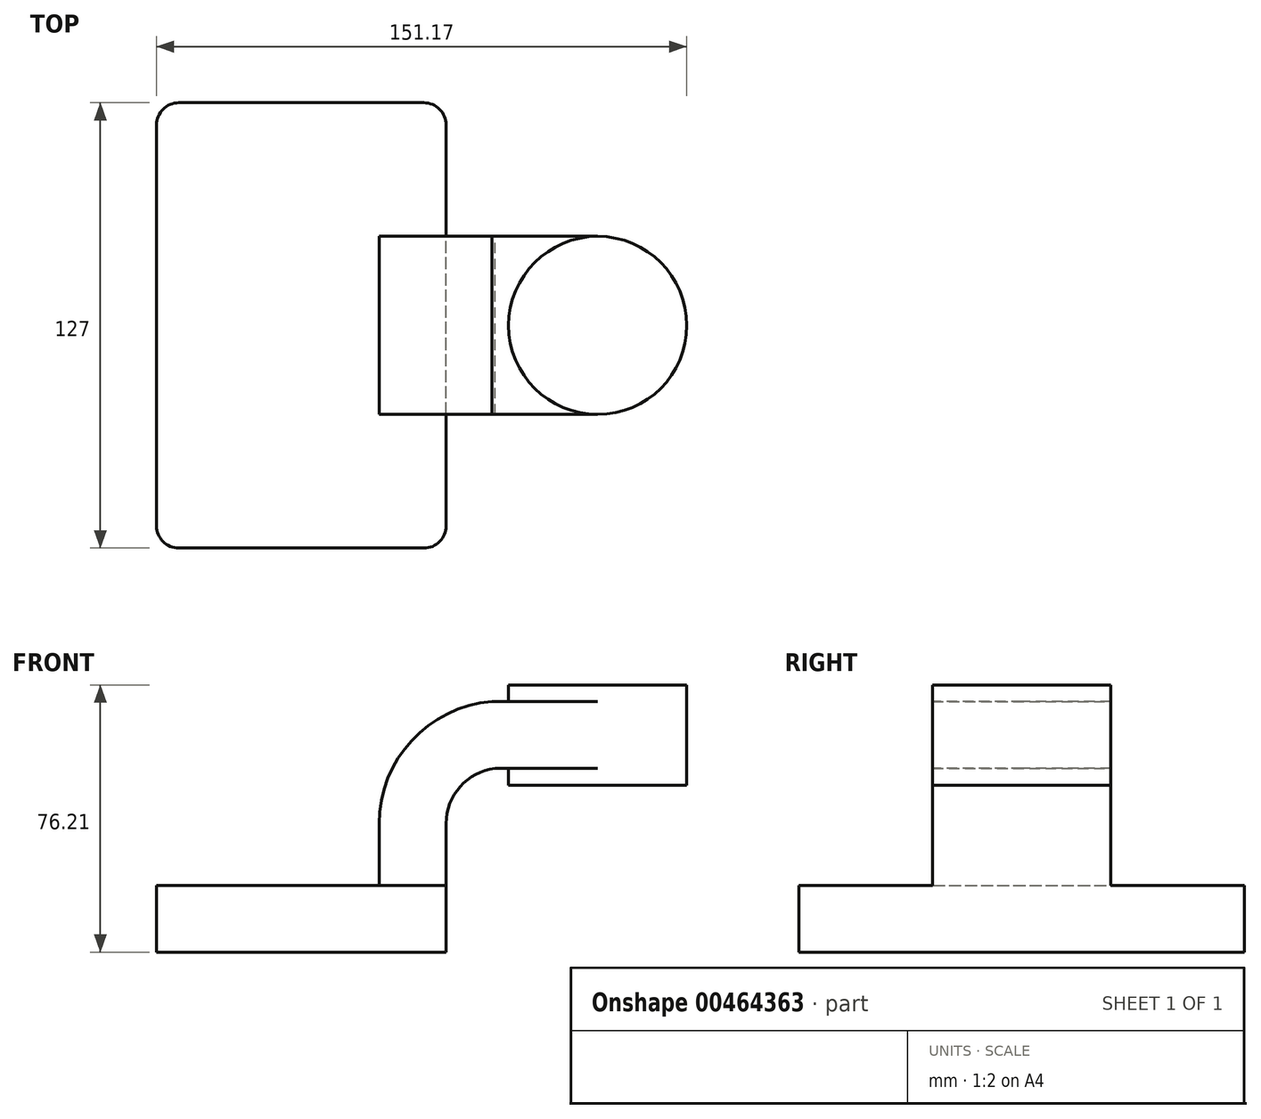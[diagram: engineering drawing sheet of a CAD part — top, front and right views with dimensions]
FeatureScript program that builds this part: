
annotation { "Feature Type Name" : "Feature", "Feature Type Description" : "" }
export const myFeature = defineFeature(function(context is Context, id is Id, definition is map)
    precondition{}
    {
        {
            var Q0;
            Q0=qCreatedBy(makeId("Front.planeOp"),FACE);
            var sketch = newSketch(context, id + "F0", { "sketchPlane" : qUnion([Q0])});
            skLineSegment(sketch, "E0.bottom", {"start": v(41.27, 9.53) * mm, "end": v(-41.28, 9.53) * mm});
            skLineSegment(sketch, "E0.top", {"start": v(41.28, -9.52) * mm, "end": v(-41.27, -9.52) * mm});
            skLineSegment(sketch, "E0.left", {"start": v(41.28, 9.53) * mm, "end": v(41.28, -9.52) * mm});
            skLineSegment(sketch, "E0.right", {"start": v(-41.28, 9.53) * mm, "end": v(-41.27, -9.52) * mm});
            skPoint(sketch, "E0.middle", {"position": v(0, 0) * mm});
            skLineSegment(sketch, "E1.bottom", {"start": v(109.9, 38.1) * mm, "end": v(59.1, 38.1) * mm});
            skLineSegment(sketch, "E1.top", {"start": v(109.9, 66.68) * mm, "end": v(59.1, 66.68) * mm});
            skLineSegment(sketch, "E1.left", {"start": v(109.9, 38.1) * mm, "end": v(109.9, 66.68) * mm});
            skLineSegment(sketch, "E1.right", {"start": v(59.1, 38.1) * mm, "end": v(59.1, 66.68) * mm});
            skPoint(sketch, "E1.middle", {"position": v(84.5, 52.39) * mm});
            skLineSegment(sketch, "E2", {"start": v(41.27, 9.53) * mm, "end": v(41.27, 27.12) * mm});
            skArc(sketch, "E3", {"start": v(41.27, 27.12) * mm, "mid": v(45.27, 37.64) * mm, "end": v(55.24, 42.88) * mm});
            skLineSegment(sketch, "E4", {"start": v(55.24, 42.88) * mm, "end": v(84.5, 42.88) * mm});
            skPoint(sketch, "E4.endSnap0", {"position": v(84.5, 38.1) * mm});
            skLineSegment(sketch, "E5.0", {"start": v(54.32, 61.93) * mm, "end": v(84.5, 61.93) * mm});
            skArc(sketch, "E5.1", {"start": v(22.23, 27.12) * mm, "mid": v(31.47, 50.79) * mm, "end": v(54.32, 61.93) * mm});
            skLineSegment(sketch, "E5.2", {"start": v(22.22, 9.53) * mm, "end": v(22.22, 27.12) * mm});
            skLineSegment(sketch, "E6", {"start": v(84.5, 38.1) * mm, "end": v(84.5, 66.68) * mm});
            skFitSpline(sketch, "E7", {"points": [v(-41.28, 9.53) * mm, v(54.32, 61.93) * mm], "startDerivative": vector(27.13, 117.02) * mm, "endDerivative": vector(129.04, -6.2) * mm});
            skSolve(sketch);
        }
        {
            var Q0;
            Q0=makeQuery(id+"F0.imprint","IMPRINT",FACE,{"disambiguationData":[TD([[makeQuery(id+"F0.imprint","IMPRINT",EDGE,{"derivedFrom":sQuery(id+"F0.wireOp",EDGE,"E0.top")}),-1.0]])]});
            extrude(context, id + "F1", {"entities" : qUnion([Q0]), "endBound" : BoundingType.SYMMETRIC, "depth" : 127 * mm});
        }
        {
            var Q0;
            {var subQ1=sQuery(id+"F0.wireOp",EDGE,"E2");Q0=makeQuery(id+"F0.imprint","IMPRINT",FACE,{"disambiguationData":[TD([[makeQuery(id+"F0.imprint","IMPRINT",EDGE,{"derivedFrom":subQ1}),1.0]])]});}
            var Q1;
            {var subQ0=sQuery(id+"F0.wireOp",EDGE,"E4");var subQ1=sQuery(id+"F0.wireOp",EDGE,"E1.right");var subQ2=makeQuery(id+"F0.imprint","INTERSECT",VERTEX,{"derivedFrom":[subQ1,subQ0]});Q1=makeQuery(id+"F0.imprint","IMPRINT",FACE,{"disambiguationData":[TD([[makeQuery(id+"F0.imprint","IMPRINT",EDGE,{"disambiguationData":[TD([[subQ2,-1.0]])],"derivedFrom":subQ1}),-1.0]])]});}
            extrude(context, id + "F2", {"entities" : qUnion([Q0, Q1]), "operationType" : NewBodyOperationType.ADD, "endBound" : BoundingType.SYMMETRIC, "depth" : 50.8 * mm});
        }
        {
            var Q0;
            Q0=makeQuery(id+"F0.imprint","IMPRINT",FACE,{"disambiguationData":[TD([[makeQuery(id+"F0.imprint","IMPRINT",EDGE,{"derivedFrom":sQuery(id+"F0.wireOp",EDGE,"E5.1")}),1.0]])]});
            extrude(context, id + "F3", {"entities" : qUnion([Q0]), "operationType" : NewBodyOperationType.ADD, "endBound" : BoundingType.SYMMETRIC, "depth" : 15.88 * mm});
        }
        {
            var Q0;
            {var subQ4=sQuery(id+"F0.wireOp",EDGE,"E1.left");Q0=makeQuery(id+"F0.imprint","IMPRINT",FACE,{"disambiguationData":[TD([[makeQuery(id+"F0.imprint","IMPRINT",EDGE,{"derivedFrom":subQ4}),1.0]])]});}
            var Q1;
            Q1=sQuery(id+"F0.wireOp",EDGE,"E6");
            revolve(context, id + "F4", {"operationType" : NewBodyOperationType.ADD, "entities" : qUnion([Q0]), "axis" : qUnion([Q1]), "revolveType" : RevolveType.FULL});
        }
        {
            var Q0;
            Q0=makeQuery(id+"F1.opExtrude","CAP_EDGE",EDGE,{"disambiguationData":[OSD([sQuery(id+"F0.wireOp",EDGE,"E0.left")])],"isStart":false});
            var Q1;
            Q1=makeQuery(id+"F1.opExtrude","CAP_EDGE",EDGE,{"disambiguationData":[OSD([sQuery(id+"F0.wireOp",EDGE,"E0.left")])],"isStart":true});
            var Q2;
            Q2=makeQuery(id+"F1.opExtrude","CAP_EDGE",EDGE,{"disambiguationData":[OSD([sQuery(id+"F0.wireOp",EDGE,"E0.right")])],"isStart":true});
            var Q3;
            Q3=makeQuery(id+"F1.opExtrude","CAP_EDGE",EDGE,{"disambiguationData":[OSD([sQuery(id+"F0.wireOp",EDGE,"E0.right")])],"isStart":false});
            fillet(context, id + "F5", {"entities" : qUnion([Q0, Q1, Q2, Q3]), "radius" : 6.35 * mm, "tangentPropagation" : true, "allowEdgeOverflow" : false});
        }
    });
